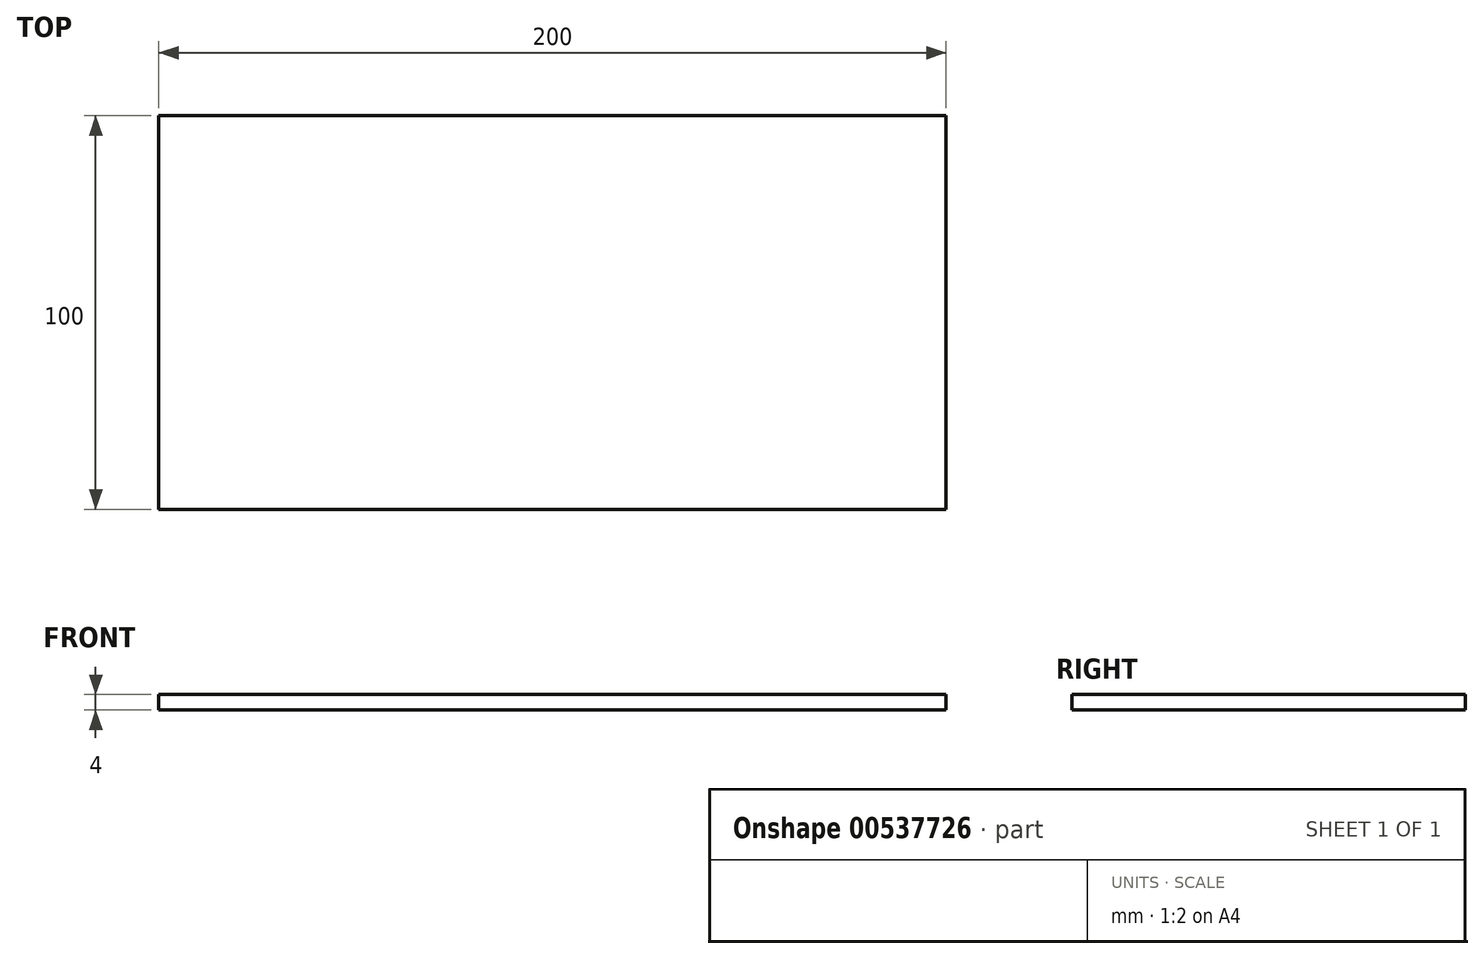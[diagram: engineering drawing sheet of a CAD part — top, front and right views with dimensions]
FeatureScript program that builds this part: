
annotation { "Feature Type Name" : "Feature", "Feature Type Description" : "" }
export const myFeature = defineFeature(function(context is Context, id is Id, definition is map)
    precondition{}
    {
        {
            var Q0;
            Q0=qCreatedBy(makeId("Top.planeOp"),FACE);
            var sketch = newSketch(context, id + "F0", { "sketchPlane" : qUnion([Q0])});
            skLineSegment(sketch, "E0.bottom", {"start": v(100, 50) * mm, "end": v(-100, 50) * mm});
            skLineSegment(sketch, "E0.top", {"start": v(100, -50) * mm, "end": v(-100, -50) * mm});
            skLineSegment(sketch, "E0.left", {"start": v(100, 50) * mm, "end": v(100, -50) * mm});
            skLineSegment(sketch, "E0.right", {"start": v(-100, 50) * mm, "end": v(-100, -50) * mm});
            skPoint(sketch, "E0.middle", {"position": v(0, 0) * mm});
            skSolve(sketch);
        }
        {
            var Q0;
            Q0=makeQuery(id+"F0.imprint","IMPRINT",FACE,{"disambiguationData":[TD([[makeQuery(id+"F0.imprint","IMPRINT",EDGE,{"derivedFrom":sQuery(id+"F0.wireOp",EDGE,"E0.bottom")}),1.0]])]});
            extrude(context, id + "F1", {"entities" : qUnion([Q0]), "depth" : 4 * mm, "offsetDistance" : 25 * mm});
        }
    });
